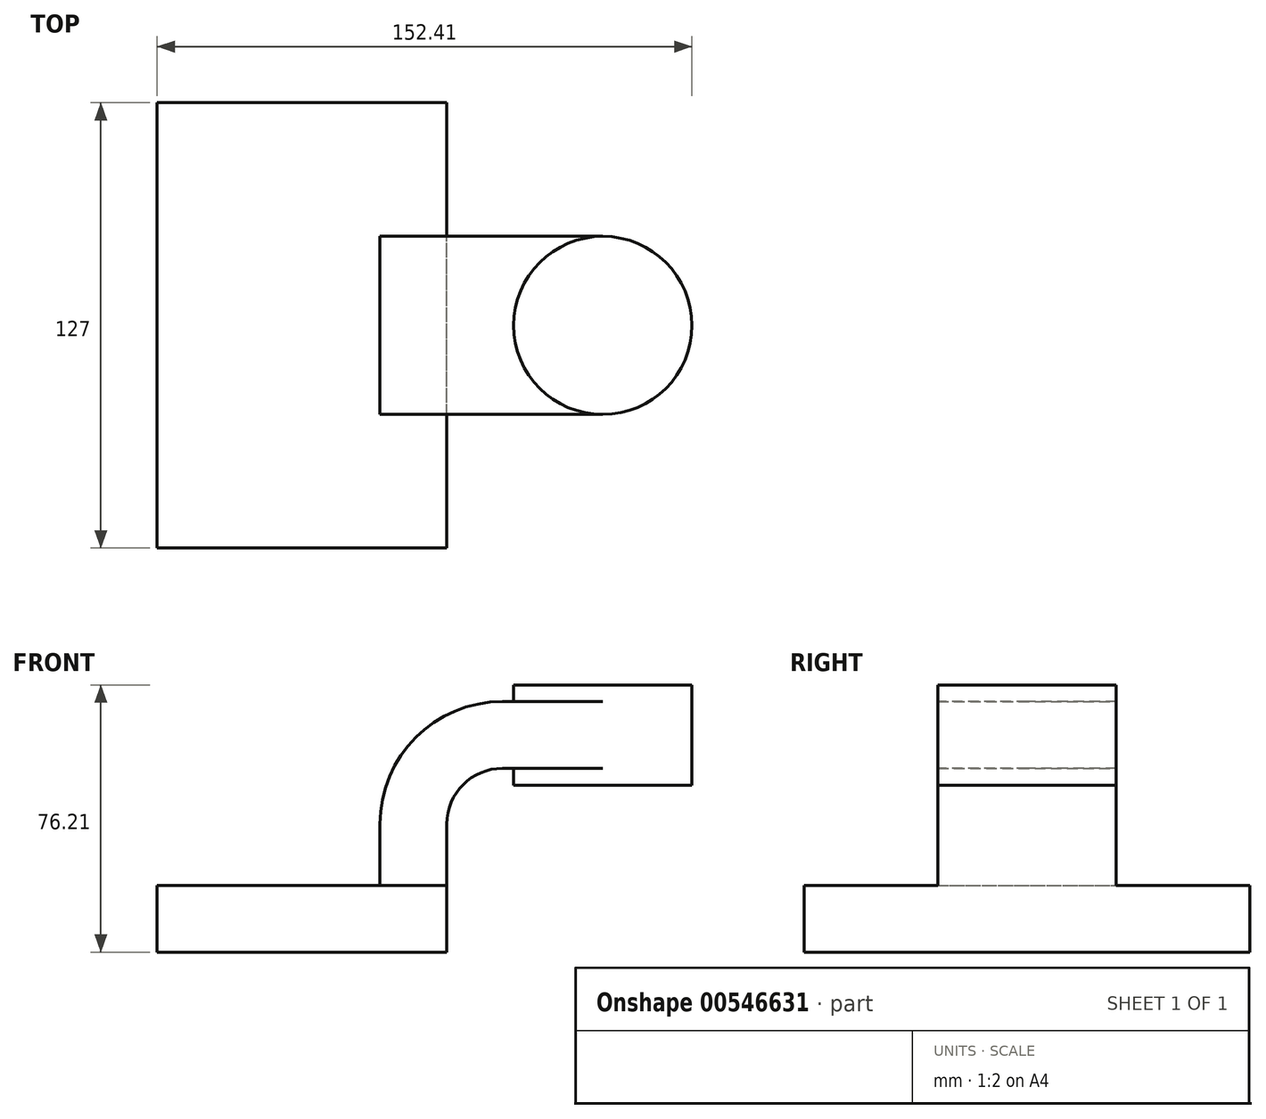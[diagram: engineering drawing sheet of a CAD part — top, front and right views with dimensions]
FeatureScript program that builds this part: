
annotation { "Feature Type Name" : "Feature", "Feature Type Description" : "" }
export const myFeature = defineFeature(function(context is Context, id is Id, definition is map)
    precondition{}
    {
        {
            var Q0;
            Q0=qCreatedBy(makeId("Front.planeOp"),FACE);
            var sketch = newSketch(context, id + "F0", { "sketchPlane" : qUnion([Q0])});
            skLineSegment(sketch, "E0.bottom", {"start": v(41.28, -9.52) * mm, "end": v(-41.28, -9.53) * mm});
            skLineSegment(sketch, "E0.top", {"start": v(41.28, 9.53) * mm, "end": v(-41.28, 9.53) * mm});
            skLineSegment(sketch, "E0.left", {"start": v(41.28, -9.52) * mm, "end": v(41.28, 9.53) * mm});
            skLineSegment(sketch, "E0.right", {"start": v(-41.28, -9.53) * mm, "end": v(-41.28, 9.53) * mm});
            skPoint(sketch, "E0.middle", {"position": v(0, 0) * mm});
            skLineSegment(sketch, "E1.bottom", {"start": v(111.12, 66.68) * mm, "end": v(60.33, 66.68) * mm});
            skLineSegment(sketch, "E1.top", {"start": v(111.12, 38.1) * mm, "end": v(60.33, 38.1) * mm});
            skLineSegment(sketch, "E1.left", {"start": v(111.12, 66.68) * mm, "end": v(111.12, 38.1) * mm});
            skLineSegment(sketch, "E1.right", {"start": v(60.33, 66.68) * mm, "end": v(60.33, 38.1) * mm});
            skPoint(sketch, "E1.middle", {"position": v(85.72, 52.39) * mm});
            skLineSegment(sketch, "E2", {"start": v(41.28, 9.53) * mm, "end": v(41.28, 27) * mm});
            skArc(sketch, "E3", {"start": v(41.27, 27) * mm, "mid": v(45.92, 38.23) * mm, "end": v(57.15, 42.88) * mm});
            skLineSegment(sketch, "E4", {"start": v(57.15, 42.88) * mm, "end": v(90.07, 42.88) * mm});
            skLineSegment(sketch, "E5.0", {"start": v(57.15, 61.93) * mm, "end": v(90.07, 61.93) * mm});
            skArc(sketch, "E5.1", {"start": v(22.23, 27) * mm, "mid": v(32.45, 51.7) * mm, "end": v(57.15, 61.93) * mm});
            skLineSegment(sketch, "E5.2", {"start": v(22.22, 9.53) * mm, "end": v(22.22, 27) * mm});
            skLineSegment(sketch, "E6", {"start": v(85.72, 38.1) * mm, "end": v(85.72, 66.68) * mm});
            skFitSpline(sketch, "E7", {"points": [v(-41.28, 9.53) * mm, v(57.15, 61.93) * mm], "startDerivative": vector(22.18, 113.2) * mm, "endDerivative": vector(171.45, -1.47) * mm});
            skSolve(sketch);
        }
        {
            var Q0;
            Q0=makeQuery(id+"F0.imprint","IMPRINT",FACE,{"disambiguationData":[TD([[makeQuery(id+"F0.imprint","IMPRINT",EDGE,{"derivedFrom":sQuery(id+"F0.wireOp",EDGE,"E0.bottom")}),-1.0]])]});
            extrude(context, id + "F1", {"entities" : qUnion([Q0]), "endBound" : BoundingType.SYMMETRIC, "depth" : 127 * mm, "offsetDistance" : 25.4 * mm});
        }
        {
            var Q0;
            {var subQ1=sQuery(id+"F0.wireOp",EDGE,"E2");Q0=makeQuery(id+"F0.imprint","IMPRINT",FACE,{"disambiguationData":[TD([[makeQuery(id+"F0.imprint","IMPRINT",EDGE,{"derivedFrom":subQ1}),1.0]])]});}
            var Q1;
            {var subQ0=sQuery(id+"F0.wireOp",EDGE,"E5.0");var subQ1=sQuery(id+"F0.wireOp",EDGE,"E1.right");var subQ2=makeQuery(id+"F0.imprint","INTERSECT",VERTEX,{"derivedFrom":[subQ1,subQ0]});Q1=makeQuery(id+"F0.imprint","IMPRINT",FACE,{"disambiguationData":[TD([[makeQuery(id+"F0.imprint","IMPRINT",EDGE,{"disambiguationData":[TD([[subQ2,-1.0]])],"derivedFrom":subQ1}),1.0]])]});}
            extrude(context, id + "F2", {"entities" : qUnion([Q0, Q1]), "operationType" : NewBodyOperationType.ADD, "endBound" : BoundingType.SYMMETRIC, "depth" : 50.8 * mm, "offsetDistance" : 25.4 * mm});
        }
        {
            var Q0;
            Q0=makeQuery(id+"F0.imprint","IMPRINT",FACE,{"disambiguationData":[TD([[makeQuery(id+"F0.imprint","IMPRINT",EDGE,{"derivedFrom":sQuery(id+"F0.wireOp",EDGE,"E5.1")}),1.0]])]});
            extrude(context, id + "F3", {"entities" : qUnion([Q0]), "operationType" : NewBodyOperationType.ADD, "endBound" : BoundingType.SYMMETRIC, "depth" : 15.88 * mm, "offsetDistance" : 25.4 * mm});
        }
        {
            var Q0;
            {var subQ4=sQuery(id+"F0.wireOp",EDGE,"E1.left");Q0=makeQuery(id+"F0.imprint","IMPRINT",FACE,{"disambiguationData":[TD([[makeQuery(id+"F0.imprint","IMPRINT",EDGE,{"derivedFrom":subQ4}),-1.0]])]});}
            var Q1;
            Q1=sQuery(id+"F0.wireOp",EDGE,"E6");
            revolve(context, id + "F4", {"operationType" : NewBodyOperationType.ADD, "entities" : qUnion([Q0]), "axis" : qUnion([Q1]), "revolveType" : RevolveType.FULL});
        }
    });
